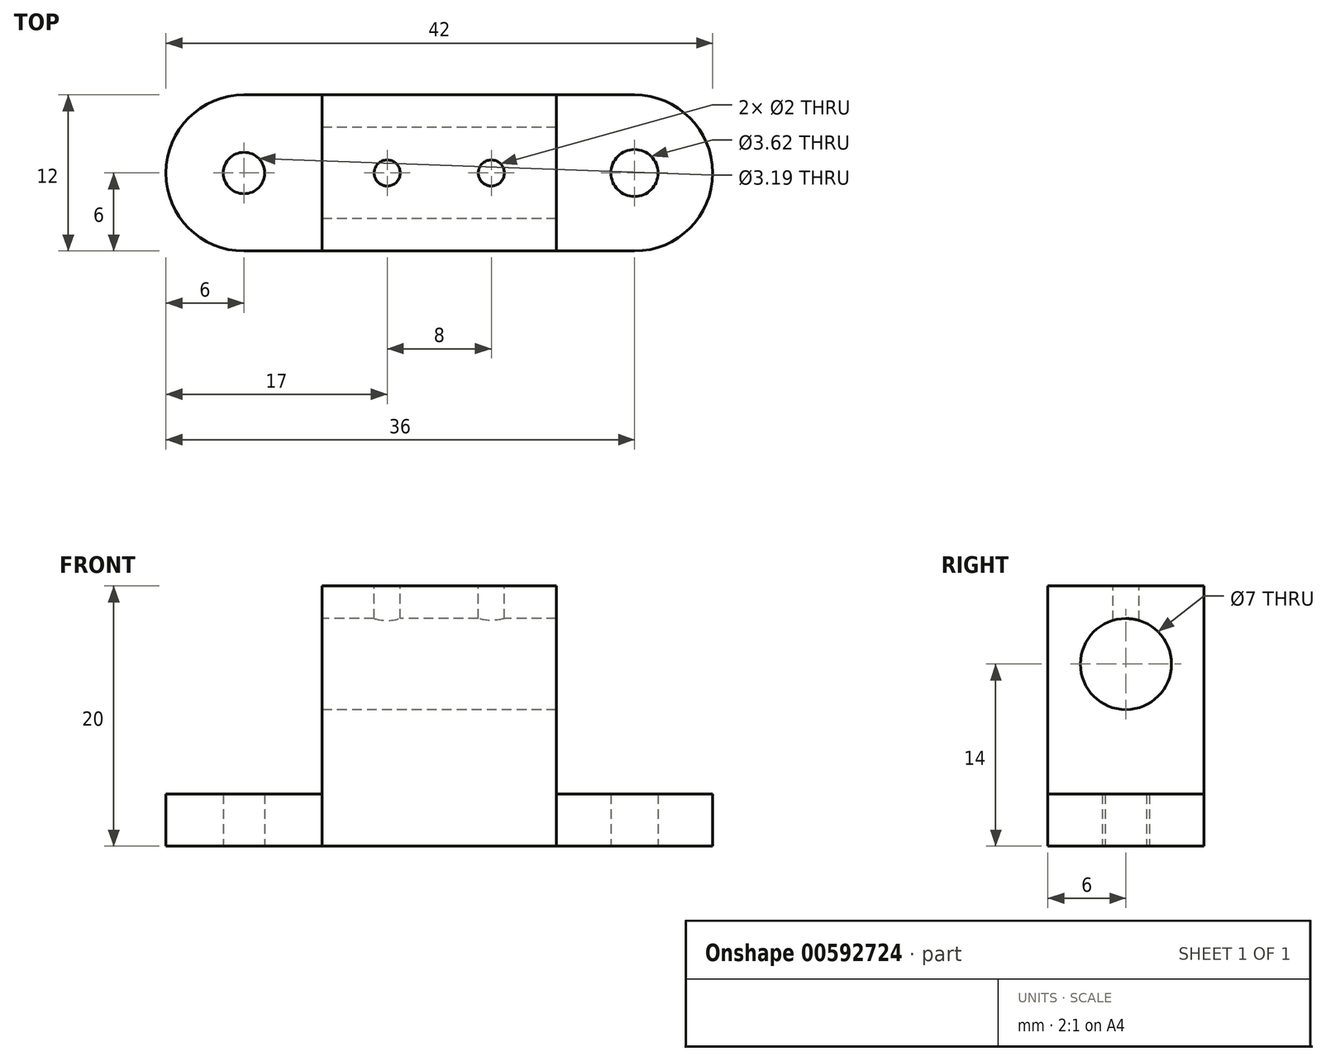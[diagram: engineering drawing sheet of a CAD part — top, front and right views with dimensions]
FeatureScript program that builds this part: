
annotation { "Feature Type Name" : "Feature", "Feature Type Description" : "" }
export const myFeature = defineFeature(function(context is Context, id is Id, definition is map)
    precondition{}
    {
        {
            var Q0;
            Q0=qCreatedBy(makeId("Top.planeOp"),FACE);
            var sketch = newSketch(context, id + "F0", { "sketchPlane" : qUnion([Q0])});
            skLineSegment(sketch, "E0.bottom", {"start": v(6, 0) * mm, "end": v(36, 0) * mm});
            skLineSegment(sketch, "E0.top", {"start": v(6, 12) * mm, "end": v(36, 12) * mm});
            skLineSegment(sketch, "E0.left", {"start": v(0, 6) * mm, "end": v(0, 6) * mm});
            skLineSegment(sketch, "E0.right", {"start": v(42, 6) * mm, "end": v(42, 6) * mm});
            skCircle(sketch, "E1", {"center": v(6, 6) * mm, "radius": 1.6 * mm});
            skPoint(sketch, "E2.visualSharp", {"position": v(0, 12) * mm});
            skArc(sketch, "E2.filletArc", {"start": v(6, 12) * mm, "mid": v(1.76, 10.24) * mm, "end": v(0, 6) * mm});
            skPoint(sketch, "E3.visualSharp", {"position": v(0, 0) * mm});
            skArc(sketch, "E3.filletArc", {"start": v(0, 6) * mm, "mid": v(1.76, 1.76) * mm, "end": v(6, 0) * mm});
            skCircle(sketch, "E4", {"center": v(36, 6) * mm, "radius": 1.81 * mm});
            skPoint(sketch, "E5.visualSharp", {"position": v(42, 12) * mm});
            skArc(sketch, "E5.filletArc", {"start": v(42, 6) * mm, "mid": v(40.24, 10.24) * mm, "end": v(36, 12) * mm});
            skPoint(sketch, "E6.visualSharp", {"position": v(42, 0) * mm});
            skArc(sketch, "E6.filletArc", {"start": v(36, 0) * mm, "mid": v(40.24, 1.76) * mm, "end": v(42, 6) * mm});
            skLineSegment(sketch, "E7", {"start": v(12, 12) * mm, "end": v(12, 0) * mm});
            skLineSegment(sketch, "E8", {"start": v(30, 12) * mm, "end": v(30, 0) * mm});
            skSolve(sketch);
        }
        {
            var Q0;
            Q0=makeQuery(id+"F0.imprint","IMPRINT",FACE,{"disambiguationData":[TD([[makeQuery(id+"F0.imprint","IMPRINT",EDGE,{"derivedFrom":sQuery(id+"F0.wireOp",EDGE,"E1")}),-1.0]])]});
            var Q1;
            Q1=makeQuery(id+"F0.imprint","IMPRINT",FACE,{"disambiguationData":[TD([[makeQuery(id+"F0.imprint","IMPRINT",EDGE,{"derivedFrom":sQuery(id+"F0.wireOp",EDGE,"E4")}),-1.0]])]});
            extrude(context, id + "F1", {"entities" : qUnion([Q0, Q1]), "depth" : 4 * mm, "offsetDistance" : 25 * mm});
        }
        {
            var Q0;
            {var subQ0=sQuery(id+"F0.wireOp",EDGE,"E7");Q0=makeQuery(id+"F0.imprint","IMPRINT",FACE,{"disambiguationData":[TD([[makeQuery(id+"F0.imprint","IMPRINT",EDGE,{"derivedFrom":subQ0}),1.0]])]});}
            extrude(context, id + "F2", {"entities" : qUnion([Q0]), "depth" : 20 * mm, "offsetDistance" : 25 * mm});
        }
        {
            var Q0;
            Q0=makeQuery(id+"F2.opExtrude","SWEPT_FACE",FACE,{"disambiguationData":[OSD([sQuery(id+"F0.wireOp",EDGE,"E7")])]});
            var sketch = newSketch(context, id + "F3", { "sketchPlane" : qUnion([Q0])});
            skCircle(sketch, "E9", {"center": v(-6, 14) * mm, "radius": 3.5 * mm});
            skSolve(sketch);
        }
        {
            var Q0;
            Q0=makeQuery(id+"F3.imprint","IMPRINT",FACE,{"disambiguationData":[TD([[makeQuery(id+"F3.imprint","IMPRINT",EDGE,{"derivedFrom":sQuery(id+"F3.wireOp",EDGE,"E9")}),1.0]])]});
            extrude(context, id + "F4", {"entities" : qUnion([Q0]), "operationType" : NewBodyOperationType.REMOVE, "oppositeDirection" : true, "depth" : 25 * mm, "offsetDistance" : 25 * mm});
        }
        {
            var Q0;
            Q0=makeQuery(id+"F2.opExtrude","CAP_FACE",FACE,{"disambiguationData":[OSD([sQuery(id+"F0.wireOp",EDGE,"E0.bottom"),sQuery(id+"F0.wireOp",EDGE,"E0.top"),sQuery(id+"F0.wireOp",EDGE,"E7"),sQuery(id+"F0.wireOp",EDGE,"E8")])],"isStart":false});
            var sketch = newSketch(context, id + "F5", { "sketchPlane" : qUnion([Q0])});
            skCircle(sketch, "E10", {"center": v(17, 6) * mm, "radius": 1 * mm});
            skCircle(sketch, "E11", {"center": v(25, 6) * mm, "radius": 1 * mm});
            skSolve(sketch);
        }
        {
            var Q0;
            Q0=makeQuery(id+"F5.imprint","IMPRINT",FACE,{"disambiguationData":[TD([[makeQuery(id+"F5.imprint","IMPRINT",EDGE,{"derivedFrom":sQuery(id+"F5.wireOp",EDGE,"E10")}),1.0]])]});
            var Q1;
            Q1=makeQuery(id+"F5.imprint","IMPRINT",FACE,{"disambiguationData":[TD([[makeQuery(id+"F5.imprint","IMPRINT",EDGE,{"derivedFrom":sQuery(id+"F5.wireOp",EDGE,"E11")}),1.0]])]});
            extrude(context, id + "F6", {"entities" : qUnion([Q0, Q1]), "operationType" : NewBodyOperationType.REMOVE, "oppositeDirection" : true, "depth" : 5 * mm, "offsetDistance" : 25 * mm});
        }
    });
